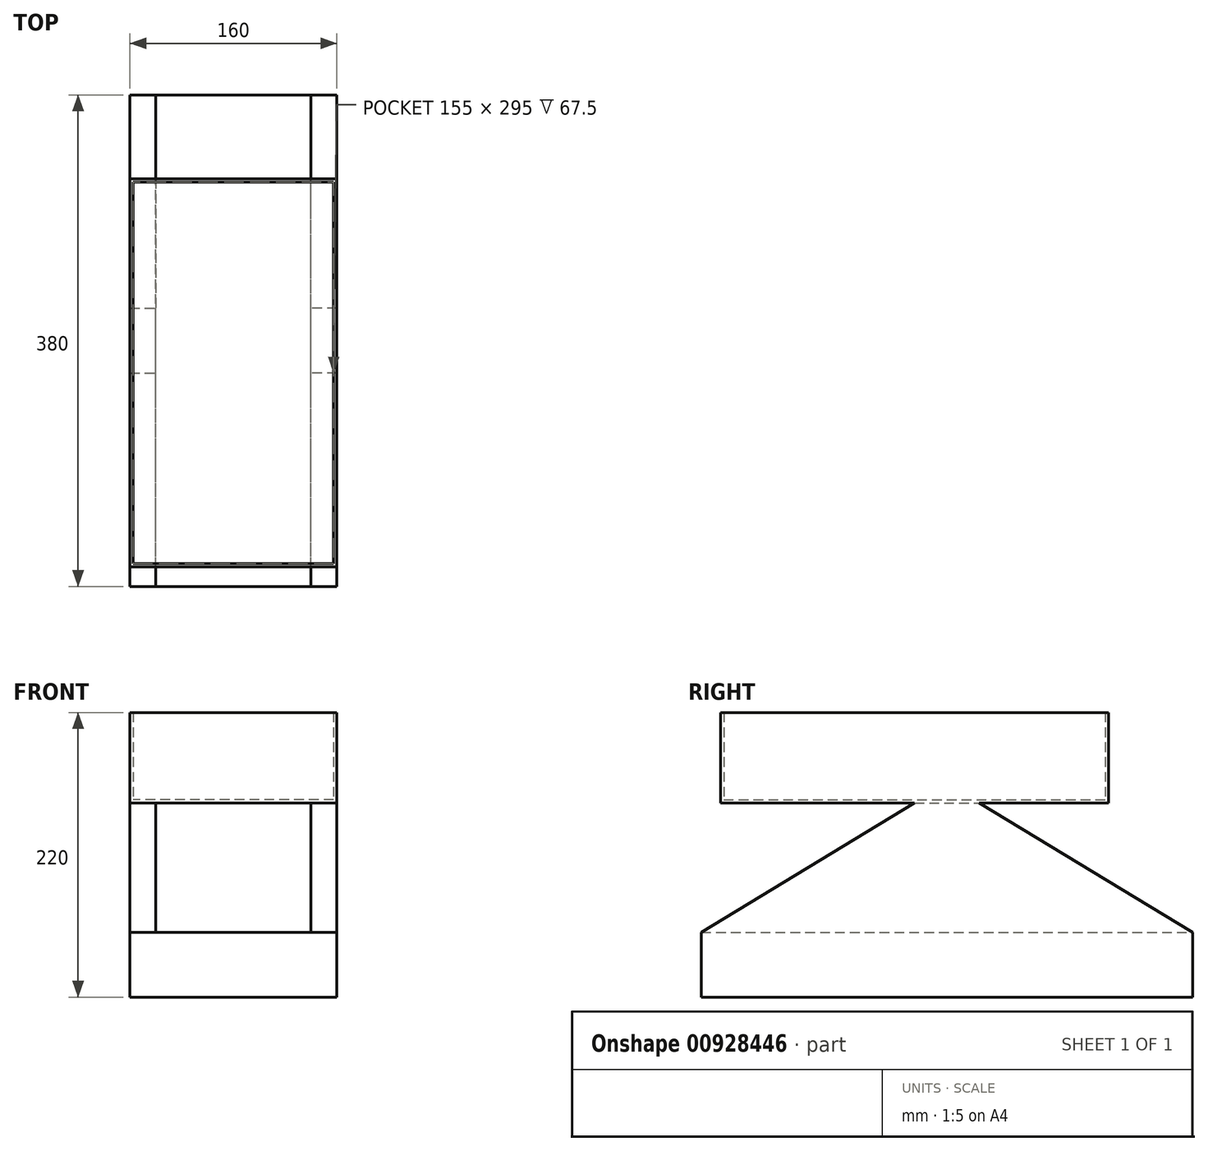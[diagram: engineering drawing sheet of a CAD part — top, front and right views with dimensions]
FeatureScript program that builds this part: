
annotation { "Feature Type Name" : "Feature", "Feature Type Description" : "" }
export const myFeature = defineFeature(function(context is Context, id is Id, definition is map)
    precondition{}
    {
        {
            var Q0;
            Q0=qCreatedBy(makeId("Top.planeOp"),FACE);
            cPlane(context, id + "F0", {"entities" : qUnion([Q0]), "cplaneType" : CPlaneType.OFFSET, "offset" : 275 * mm, "width" : 150 * mm, "height" : 150 * mm});
        }
        {
            var Q0;
            Q0=qCreatedBy(id+"F0.planeOp",FACE);
            var sketch = newSketch(context, id + "F1", { "sketchPlane" : qUnion([Q0])});
            skLineSegment(sketch, "E0.bottom", {"start": v(-80, 190) * mm, "end": v(80, 190) * mm});
            skLineSegment(sketch, "E0.top", {"start": v(-80, -190) * mm, "end": v(80, -190) * mm});
            skLineSegment(sketch, "E0.left", {"start": v(-80, 190) * mm, "end": v(-80, -190) * mm});
            skLineSegment(sketch, "E0.right", {"start": v(80, 190) * mm, "end": v(80, -190) * mm});
            skLineSegment(sketch, "E1", {"start": v(-80, 190) * mm, "end": v(80, -190) * mm, "construction": true});
            skLineSegment(sketch, "E2", {"start": v(80, 190) * mm, "end": v(-80, -190) * mm, "construction": true});
            skPoint(sketch, "E3", {"position": v(0, 0) * mm});
            skSolve(sketch);
        }
        {
            var Q0;
            Q0=makeQuery(id+"F1.imprint","IMPRINT",FACE,{"disambiguationData":[TD([[makeQuery(id+"F1.imprint","IMPRINT",EDGE,{"derivedFrom":sQuery(id+"F1.wireOp",EDGE,"E0.bottom")}),-1.0]])]});
            extrude(context, id + "F2", {"entities" : qUnion([Q0]), "oppositeDirection" : true, "depth" : 50 * mm, "offsetDistance" : 25 * mm});
        }
        {
            var Q0;
            Q0=makeQuery(id+"F2.opExtrude","CAP_FACE",FACE,{"disambiguationData":[OSD([sQuery(id+"F1.wireOp",EDGE,"E0.bottom"),sQuery(id+"F1.wireOp",EDGE,"E0.top"),sQuery(id+"F1.wireOp",EDGE,"E0.left"),sQuery(id+"F1.wireOp",EDGE,"E0.right")])],"isStart":true});
            var sketch = newSketch(context, id + "F3", { "sketchPlane" : qUnion([Q0])});
            skLineSegment(sketch, "E4.bottom", {"start": v(-80, -190) * mm, "end": v(-60, -190) * mm});
            skLineSegment(sketch, "E4.top", {"start": v(-80, -90) * mm, "end": v(-60, -90) * mm});
            skLineSegment(sketch, "E4.left", {"start": v(-80, -190) * mm, "end": v(-80, -90) * mm});
            skLineSegment(sketch, "E4.right", {"start": v(-60, -190) * mm, "end": v(-60, -90) * mm});
            skLineSegment(sketch, "E5.bottom", {"start": v(80, -190) * mm, "end": v(60, -190) * mm});
            skLineSegment(sketch, "E5.top", {"start": v(80, -90) * mm, "end": v(60, -90) * mm});
            skLineSegment(sketch, "E5.left", {"start": v(80, -190) * mm, "end": v(80, -90) * mm});
            skLineSegment(sketch, "E5.right", {"start": v(60, -190) * mm, "end": v(60, -90) * mm});
            skSolve(sketch);
        }
        {
            var Q0;
            {var subQ3=sQuery(id+"F3.wireOp",EDGE,"E4.top");Q0=makeQuery(id+"F3.imprint","IMPRINT",FACE,{"disambiguationData":[TD([[makeQuery(id+"F3.imprint","IMPRINT",EDGE,{"derivedFrom":subQ3}),1.0]])]});}
            cPlane(context, id + "F4", {"entities" : qUnion([Q0]), "cplaneType" : CPlaneType.OFFSET, "offset" : 100 * mm, "width" : 150 * mm, "height" : 150 * mm});
        }
        {
            var Q0;
            Q0=qCreatedBy(id+"F4.planeOp",FACE);
            var sketch = newSketch(context, id + "F5", { "sketchPlane" : qUnion([Q0])});
            skLineSegment(sketch, "E6.bottom", {"start": v(-80, -25) * mm, "end": v(-60, -25) * mm});
            skLineSegment(sketch, "E6.top", {"start": v(-80, 25) * mm, "end": v(-60, 25) * mm});
            skLineSegment(sketch, "E6.right", {"start": v(-60, -25) * mm, "end": v(-60, 25) * mm});
            skLineSegment(sketch, "E7.bottom", {"start": v(80, -25) * mm, "end": v(60, -25) * mm});
            skLineSegment(sketch, "E7.top", {"start": v(80, 25) * mm, "end": v(60, 25) * mm});
            skLineSegment(sketch, "E7.left", {"start": v(80, -25) * mm, "end": v(80, 0) * mm});
            skLineSegment(sketch, "E7.right", {"start": v(60, -25) * mm, "end": v(60, 25) * mm});
            skLineSegment(sketch, "E8.0", {"start": v(80, 190) * mm, "end": v(80, -190) * mm, "construction": true});
            skLineSegment(sketch, "E9", {"start": v(80, 0) * mm, "end": v(80, 25) * mm});
            skLineSegment(sketch, "E10.0", {"start": v(-80, 190) * mm, "end": v(-80, -190) * mm, "construction": true});
            skLineSegment(sketch, "E11", {"start": v(-80, 25) * mm, "end": v(-80, -25) * mm});
            skSolve(sketch);
        }
        {
            var Q1;
            Q1=makeQuery(id+"F3.imprint","IMPRINT",FACE,{"disambiguationData":[TD([[makeQuery(id+"F3.imprint","IMPRINT",EDGE,{"derivedFrom":sQuery(id+"F3.wireOp",EDGE,"E5.bottom")}),1.0]])]});
            var Q2;
            Q2=makeQuery(id+"F5.imprint","IMPRINT",FACE,{"disambiguationData":[TD([[makeQuery(id+"F5.imprint","IMPRINT",EDGE,{"derivedFrom":sQuery(id+"F5.wireOp",EDGE,"E7.bottom")}),-1.0]])]});
            loft(context, id + "F6", {"operationType" : NewBodyOperationType.ADD, "sheetProfilesArray" : [{ "sheetProfileEntities" : qUnion([Q1]) }, { "sheetProfileEntities" : qUnion([Q2]) }]});
        }
        {
            var Q1;
            Q1=makeQuery(id+"F3.imprint","IMPRINT",FACE,{"disambiguationData":[TD([[makeQuery(id+"F3.imprint","IMPRINT",EDGE,{"derivedFrom":sQuery(id+"F3.wireOp",EDGE,"E4.bottom")}),1.0]])]});
            var Q2;
            Q2=makeQuery(id+"F5.imprint","IMPRINT",FACE,{"disambiguationData":[TD([[makeQuery(id+"F5.imprint","IMPRINT",EDGE,{"derivedFrom":sQuery(id+"F5.wireOp",EDGE,"E6.bottom")}),1.0]])]});
            loft(context, id + "F7", {"operationType" : NewBodyOperationType.ADD, "sheetProfilesArray" : [{ "sheetProfileEntities" : qUnion([Q1]) }, { "sheetProfileEntities" : qUnion([Q2]) }]});
        }
        {
            var Q0;
            Q0=makeQuery(id+"F6.opLoft","CAP_FACE",FACE,{"disambiguationData":[OSD([makeQuery(id+"F5.imprint","IMPRINT",FACE,{"disambiguationData":[TD([[makeQuery(id+"F5.imprint","IMPRINT",EDGE,{"derivedFrom":sQuery(id+"F5.wireOp",EDGE,"E7.bottom")}),-1.0]])]})])],"isStart":true});
            var Q1;
            Q1=makeQuery(id+"F7.opLoft","CAP_FACE",FACE,{"disambiguationData":[OSD([makeQuery(id+"F5.imprint","IMPRINT",FACE,{"disambiguationData":[TD([[makeQuery(id+"F5.imprint","IMPRINT",EDGE,{"derivedFrom":sQuery(id+"F5.wireOp",EDGE,"E6.bottom")}),1.0]])]})])],"isStart":true});
            cPlane(context, id + "F8", {"entities" : qUnion([Q0, Q1]), "cplaneType" : CPlaneType.MID_PLANE, "offset" : 25 * mm, "width" : 150 * mm, "height" : 150 * mm});
        }
        {
            var Q0;
            Q0=qCreatedBy(id+"F8.planeOp",FACE);
            var sketch = newSketch(context, id + "F9", { "sketchPlane" : qUnion([Q0])});
            skLineSegment(sketch, "E12.bottom", {"start": v(80, -175) * mm, "end": v(-80, -175) * mm});
            skLineSegment(sketch, "E12.top", {"start": v(80, 125) * mm, "end": v(-80, 125) * mm});
            skLineSegment(sketch, "E12.left", {"start": v(80, -175) * mm, "end": v(80, 125) * mm});
            skLineSegment(sketch, "E12.right", {"start": v(-80, -175) * mm, "end": v(-80, -25) * mm});
            skLineSegment(sketch, "E13", {"start": v(-80, -25) * mm, "end": v(-80, 125) * mm});
            skSolve(sketch);
        }
        {
            var Q0;
            Q0 = qSketchRegion(id + "F9", true);
            extrude(context, id + "F10", {"entities" : qUnion([Q0]), "depth" : 70 * mm, "offsetDistance" : 25 * mm});
        }
        {
            var Q0;
            Q0=makeQuery(id+"F10.opExtrude","CAP_FACE",FACE,{"disambiguationData":[OSD([sQuery(id+"F9.wireOp",EDGE,"E12.bottom"),sQuery(id+"F9.wireOp",EDGE,"E12.top"),sQuery(id+"F9.wireOp",EDGE,"E12.left"),sQuery(id+"F9.wireOp",EDGE,"E12.right"),sQuery(id+"F9.wireOp",EDGE,"E13")])],"isStart":false});
            shell(context, id + "F11", {"entities" : qUnion([Q0]), "thickness" : 2.5 * mm});
        }
        {
            var Q0;
            Q0=makeQuery(id+"F6.boolean.opBoolean","MERGE",FACE,{"derivedFrom":[makeQuery(id+"F2.opExtrude","SWEPT_FACE",FACE,{"disambiguationData":[OSD([sQuery(id+"F1.wireOp",EDGE,"E0.right")])]}),makeQuery(id+"F6.opLoft","SWEPT_FACE",FACE,{"disambiguationData":[OSD([sQuery(id+"F3.wireOp",EDGE,"E5.bottom"),sQuery(id+"F3.wireOp",EDGE,"E5.left"),sQuery(id+"F5.wireOp",EDGE,"E7.bottom"),sQuery(id+"F5.wireOp",EDGE,"E7.left"),sQuery(id+"F5.wireOp",EDGE,"E9")])]})]});
            var sketch = newSketch(context, id + "F12", { "sketchPlane" : qUnion([Q0])});
            skLineSegment(sketch, "E14.0", {"start": v(-90, 275) * mm, "end": v(25, 375) * mm});
            skLineSegment(sketch, "E15.0", {"start": v(190, 275) * mm, "end": v(-90, 275) * mm});
            skLineSegment(sketch, "E16", {"start": v(25, 375) * mm, "end": v(190, 275) * mm});
            skSolve(sketch);
        }
        {
            var Q0;
            Q0 = qSketchRegion(id + "F12", true);
            extrude(context, id + "F13", {"entities" : qUnion([Q0]), "operationType" : NewBodyOperationType.ADD, "oppositeDirection" : true, "depth" : 20 * mm, "offsetDistance" : 25 * mm});
        }
        {
            var Q0;
            {var subQ0=sQuery(id+"F1.wireOp",EDGE,"E0.left");Q0=makeQuery(id+"F7.boolean.opBoolean","MERGE",FACE,{"derivedFrom":[makeQuery(id+"F2.opExtrude","SWEPT_FACE",FACE,{"disambiguationData":[OSD([subQ0])]}),makeQuery(id+"F7.opLoft","SWEPT_FACE",FACE,{"disambiguationData":[OSD([subQ0,sQuery(id+"F3.wireOp",EDGE,"E4.bottom"),sQuery(id+"F3.wireOp",EDGE,"E4.top"),sQuery(id+"F3.wireOp",EDGE,"E4.left"),sQuery(id+"F5.wireOp",EDGE,"E6.bottom"),sQuery(id+"F5.wireOp",EDGE,"E6.top"),sQuery(id+"F5.wireOp",EDGE,"E11")])]})]});}
            var sketch = newSketch(context, id + "F14", { "sketchPlane" : qUnion([Q0])});
            skLineSegment(sketch, "E17.0", {"start": v(90, 275) * mm, "end": v(-25, 375) * mm});
            skLineSegment(sketch, "E18.0", {"start": v(-190, 275) * mm, "end": v(90, 275) * mm});
            skLineSegment(sketch, "E19", {"start": v(-190, 275) * mm, "end": v(-25, 375) * mm});
            skSolve(sketch);
        }
        {
            var Q0;
            Q0=makeQuery(id+"F14.imprint","IMPRINT",FACE,{"disambiguationData":[TD([[makeQuery(id+"F14.imprint","IMPRINT",EDGE,{"derivedFrom":sQuery(id+"F14.wireOp",EDGE,"E17.0")}),1.0]])]});
            extrude(context, id + "F15", {"entities" : qUnion([Q0]), "operationType" : NewBodyOperationType.ADD, "oppositeDirection" : true, "depth" : 20 * mm, "offsetDistance" : 25 * mm});
        }
    });
